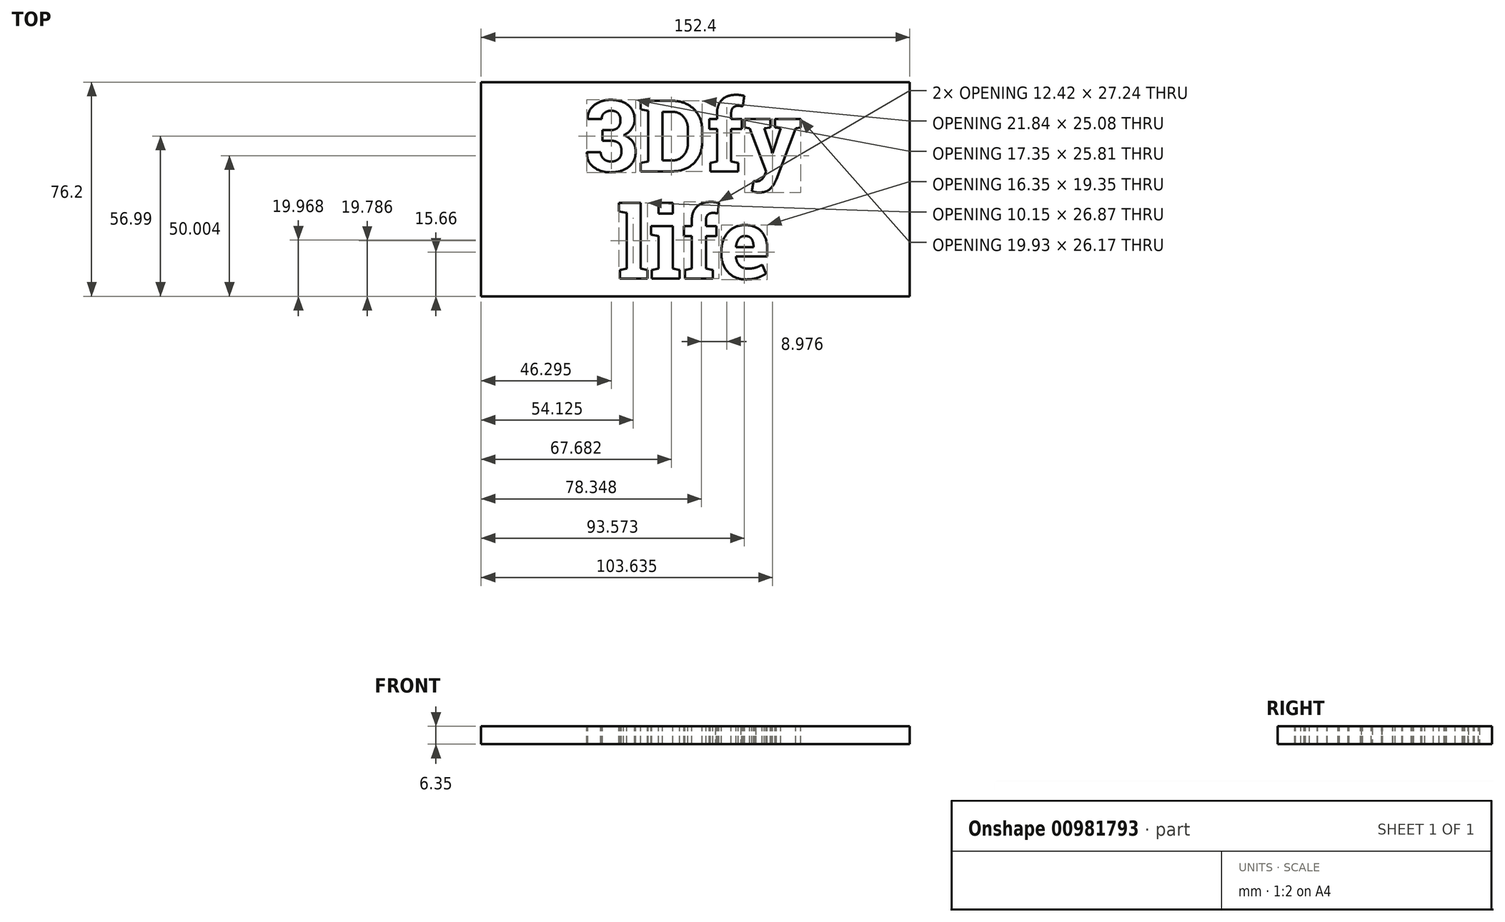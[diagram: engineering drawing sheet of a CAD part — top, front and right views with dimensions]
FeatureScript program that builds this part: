
annotation { "Feature Type Name" : "Feature", "Feature Type Description" : "" }
export const myFeature = defineFeature(function(context is Context, id is Id, definition is map)
    precondition{}
    {
        {
            var Q0;
            Q0=qCreatedBy(makeId("Top.planeOp"),FACE);
            var sketch = newSketch(context, id + "F0", { "sketchPlane" : qUnion([Q0])});
            skLineSegment(sketch, "E0.bottom", {"start": v(0, 0) * mm, "end": v(152.4, 0) * mm});
            skLineSegment(sketch, "E0.top", {"start": v(0, 76.2) * mm, "end": v(152.4, 76.2) * mm});
            skLineSegment(sketch, "E0.left", {"start": v(0, 0) * mm, "end": v(0, 76.2) * mm});
            skLineSegment(sketch, "E0.right", {"start": v(152.4, 0) * mm, "end": v(152.4, 76.2) * mm});
            skSolve(sketch);
        }
        {
            var Q0;
            Q0=makeQuery(id+"F0.imprint","IMPRINT",FACE,{"disambiguationData":[TD([[makeQuery(id+"F0.imprint","IMPRINT",EDGE,{"derivedFrom":sQuery(id+"F0.wireOp",EDGE,"E0.bottom")}),1.0]])]});
            extrude(context, id + "F1", {"entities" : qUnion([Q0]), "depth" : 6.35 * mm, "offsetDistance" : 25.4 * mm});
        }
        {
            var Q0;
            Q0=makeQuery(id+"F1.opExtrude","CAP_FACE",FACE,{"disambiguationData":[OSD([sQuery(id+"F0.wireOp",EDGE,"E0.bottom"),sQuery(id+"F0.wireOp",EDGE,"E0.top"),sQuery(id+"F0.wireOp",EDGE,"E0.left"),sQuery(id+"F0.wireOp",EDGE,"E0.right")])],"isStart":false});
            var sketch = newSketch(context, id + "F2", { "sketchPlane" : qUnion([Q0])});
            skText(sketch, "E1", { "text": "3Dfy\n", "fontName": "RobotoSlab-Bold.ttf"});
            skPoint(sketch, "E2", {"position": v(36.64, 57.15) * mm});
            skLineSegment(sketch, "E3", {"start": v(0, 57.15) * mm, "end": v(152.4, 57.15) * mm, "construction": true});
            skLineSegment(sketch, "E4", {"start": v(0, 19.05) * mm, "end": v(152.4, 19.05) * mm, "construction": true});
            skLineSegment(sketch, "E5", {"start": v(76.2, 76.2) * mm, "end": v(76.2, 0) * mm, "construction": true});
            skText(sketch, "E6", { "text": "life", "fontName": "RobotoSlab-Bold.ttf"});
            skPoint(sketch, "E7", {"position": v(48.5, 19.05) * mm});
            const initialGuessF2  = {"E1": [0.03664, 0.04445, 1, 0, 0.0254], "E6": [0.0485, 0.00635, 1, 0, 0.0254]};
            skSetInitialGuess(sketch, initialGuessF2);
            skSolve(sketch);
        }
        {
            var Q0;
            Q0 = qSketchRegion(id + "F2", true);
            extrude(context, id + "F3", {"entities" : qUnion([Q0]), "operationType" : NewBodyOperationType.REMOVE, "endBound" : BoundingType.THROUGH_ALL, "oppositeDirection" : true, "depth" : 25.4 * mm, "offsetDistance" : 25.4 * mm});
        }
    });
